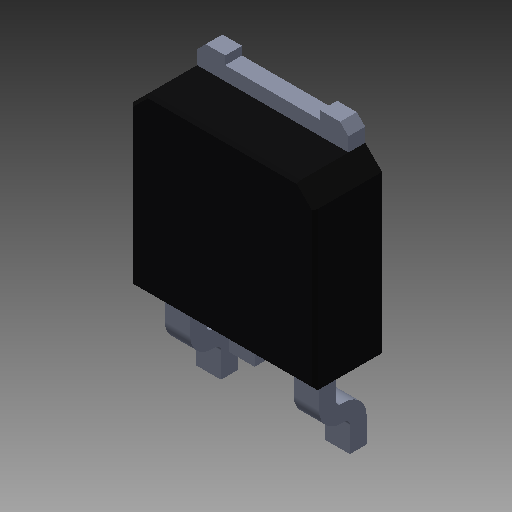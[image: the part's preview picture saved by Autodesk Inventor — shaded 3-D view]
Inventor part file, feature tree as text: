
AUTODESK INVENTOR PART (.ipt)
format: ipt  version: 2019 (Build 230136000, 136)  size: 211,456 bytes
history: native  units: mm
features: chamfer x1, imported_body x1
ambient origin geometry x8: Origin, YZ Plane, XZ Plane, XY Plane, X Axis, Y Axis, Z Axis, Center Point
bodies: Body1 (feature_tree)
feature tree (2):
  chamfer  "Fase4"  [1 undecoded]
  imported_body  "Base1"
note: 1 required parameter value undecoded (feature->parameter linkage not recoverable at this tier; creation-order binding heuristic only, values carry confidence <= 0.55)
